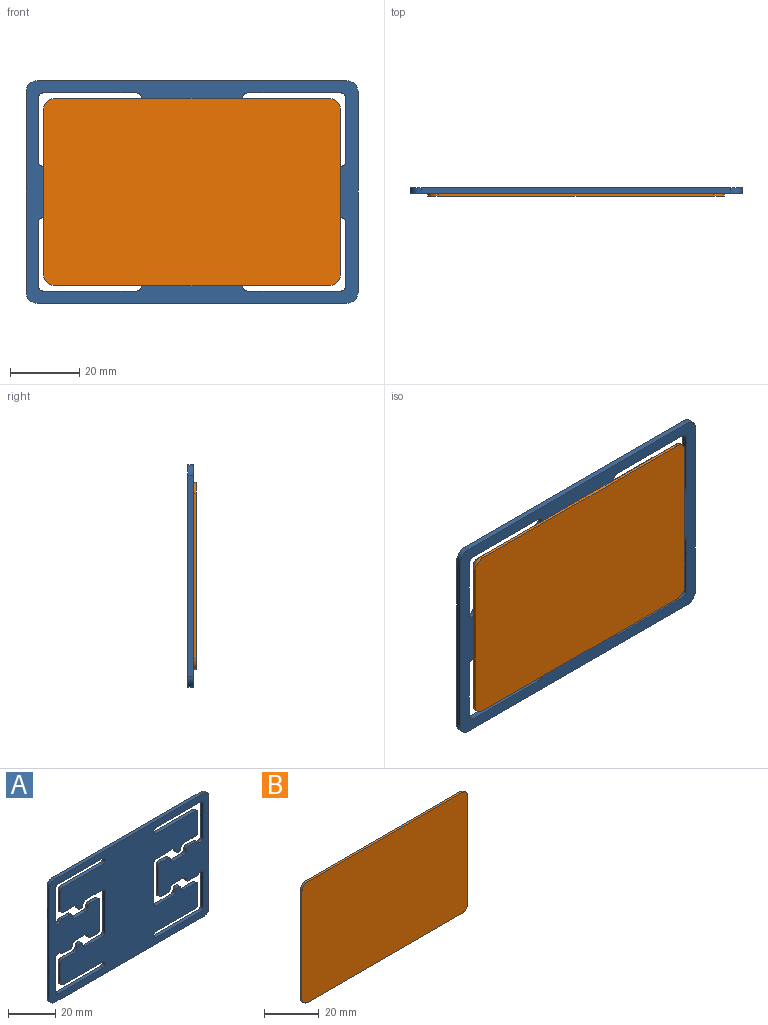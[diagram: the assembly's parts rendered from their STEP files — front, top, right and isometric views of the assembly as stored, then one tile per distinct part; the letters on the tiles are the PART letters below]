
ASSEMBLY  parts=2 mates=1
PART A: 110 faces, bbox 95.8x1.6x64.1 mm
  f0: plane 95.76x64.14mm, normal (0,1,0), area 4997.3mm2, adj f2,f3,f4,f5,f6,f7,f8,f9
  f1: plane 95.76x64.14mm, normal (0,-1,0), area 4997.3mm2, adj f2,f3,f4,f5,f6,f7,f8,f9
  f2: cylinder r=3.17mm len=3.18mm, axis (0,1,0), area 8mm2, adj f0,f1,f3,f9
  f3: plane 89.41x1.6mm, normal (0,0,-1), area 143.1mm2, adj f0,f1,f2,f4
  f4: cylinder r=3.17mm len=3.18mm, axis (0,-1,0), area 8mm2, adj f0,f1,f3,f5
  f5: plane 57.79x1.6mm, normal (1,0,0), area 92.5mm2, adj f0,f1,f4,f6
  f6: cylinder r=3.17mm len=3.18mm, axis (0,1,0), area 8mm2, adj f0,f1,f5,f7
  f7: plane 89.41x1.6mm, normal (0,0,1), area 143.1mm2, adj f0,f1,f6,f8
  f8: cylinder r=3.17mm len=3.18mm, axis (0,-1,0), area 8mm2, adj f0,f1,f7,f9
  f9: plane 57.79x1.6mm, normal (-1,0,0), area 92.5mm2, adj f0,f1,f2,f8
  f10: plane 3.81x1.6mm, normal (0,0,-1), area 6.1mm2, adj f0,f1,f54,f55
  f11: plane 14.82x1.6mm, normal (1,0,0), area 23.7mm2, adj f0,f1,f46,f54
  f12: plane 3.81x1.6mm, normal (0,0,1), area 6.1mm2, adj f0,f1,f46,f47
  f13: cylinder r=1.59mm len=1.6mm, axis (0,1,0), area 4mm2, adj f0,f1,f14,f47
  f14: plane 6.35x1.6mm, normal (0,0,1), area 10.2mm2, adj f0,f1,f13,f15
  f15: cylinder r=1.59mm len=1.6mm, axis (0,1,0), area 4mm2, adj f0,f1,f14,f49
  f16: plane 4.24x1.6mm, normal (0,0,1), area 6.8mm2, adj f0,f1,f49,f56
  f17: cylinder r=1.59mm len=2.96mm, axis (0,1,0), area 6.7mm2, adj f0,f1,f18,f56
  f18: plane 17.99x1.6mm, normal (1,0,0), area 28.8mm2, adj f0,f1,f17,f19
  f19: cylinder r=1.59mm len=1.6mm, axis (0,1,0), area 4mm2, adj f0,f1,f18,f20
  f20: plane 26.67x1.6mm, normal (0,0,-1), area 42.7mm2, adj f0,f1,f19,f21
  f21: cylinder r=1.59mm len=3.18mm, axis (0,1,0), area 8mm2, adj f0,f1,f20,f22
  f22: plane 23.5x1.6mm, normal (0,0,1), area 37.6mm2, adj f0,f1,f21,f50
  f23: plane 10.05x1.6mm, normal (-1,0,0), area 16.1mm2, adj f0,f1,f50,f57
  f24: plane 6.99x1.6mm, normal (0,0,-1), area 11.2mm2, adj f0,f1,f25,f57
  f25: cylinder r=1.59mm len=1.6mm, axis (0,1,0), area 4mm2, adj f0,f1,f24,f48
  f26: cylinder r=1.59mm len=1.6mm, axis (0,1,0), area 4mm2, adj f0,f1,f27,f48
  f27: plane 10.16x1.6mm, normal (0,0,-1), area 16.3mm2, adj f0,f1,f26,f28
  f28: cylinder r=1.59mm len=1.6mm, axis (0,1,0), area 4mm2, adj f0,f1,f27,f29
  f29: plane 21.17x1.6mm, normal (-1,0,0), area 33.9mm2, adj f0,f1,f28,f30
  f30: cylinder r=1.59mm len=1.6mm, axis (0,1,0), area 4mm2, adj f0,f1,f29,f31
  f31: plane 10.16x1.6mm, normal (0,0,1), area 16.3mm2, adj f0,f1,f30,f32
  f32: cylinder r=1.59mm len=1.6mm, axis (0,1,0), area 4mm2, adj f0,f1,f31,f53
  f33: cylinder r=1.59mm len=1.6mm, axis (0,1,0), area 4mm2, adj f0,f1,f34,f53
  f34: plane 6.99x1.6mm, normal (0,0,1), area 11.2mm2, adj f0,f1,f33,f59
  f35: plane 10.05x1.6mm, normal (-1,0,0), area 16.1mm2, adj f0,f1,f51,f59
  f36: plane 23.5x1.6mm, normal (0,0,-1), area 37.6mm2, adj f0,f1,f37,f51
  f37: cylinder r=1.59mm len=3.18mm, axis (0,1,0), area 8mm2, adj f0,f1,f36,f38
  f38: plane 26.67x1.6mm, normal (0,0,1), area 42.7mm2, adj f0,f1,f37,f39
  f39: cylinder r=1.59mm len=1.6mm, axis (0,1,0), area 4mm2, adj f0,f1,f38,f40
  f40: plane 17.99x1.6mm, normal (1,0,0), area 28.8mm2, adj f0,f1,f39,f41
  f41: cylinder r=1.59mm len=2.96mm, axis (0,1,0), area 6.7mm2, adj f0,f1,f40,f58
  f42: plane 4.24x1.6mm, normal (0,0,-1), area 6.8mm2, adj f0,f1,f52,f58
  f43: cylinder r=1.59mm len=1.6mm, axis (0,1,0), area 4mm2, adj f0,f1,f44,f52
  f44: plane 6.35x1.6mm, normal (0,0,-1), area 10.2mm2, adj f0,f1,f43,f45
  f45: cylinder r=1.59mm len=1.6mm, axis (0,1,0), area 4mm2, adj f0,f1,f44,f55
  f46: cylinder r=1.59mm len=1.6mm, axis (0,1,0), area 4mm2, adj f0,f1,f11,f12
  f47: cylinder r=1.59mm len=1.6mm, axis (0,1,0), area 4mm2, adj f0,f1,f12,f13
  f48: cylinder r=1.59mm len=3.18mm, axis (0,1,0), area 8mm2, adj f0,f1,f25,f26
  f49: cylinder r=1.59mm len=1.6mm, axis (0,1,0), area 4mm2, adj f0,f1,f15,f16
  f50: cylinder r=1.59mm len=1.6mm, axis (0,1,0), area 4mm2, adj f0,f1,f22,f23
  f51: cylinder r=1.59mm len=1.6mm, axis (0,1,0), area 4mm2, adj f0,f1,f35,f36
  f52: cylinder r=1.59mm len=1.6mm, axis (0,1,0), area 4mm2, adj f0,f1,f42,f43
  f53: cylinder r=1.59mm len=3.18mm, axis (0,1,0), area 8mm2, adj f0,f1,f32,f33
  f54: cylinder r=1.59mm len=1.6mm, axis (0,-1,0), area 4mm2, adj f0,f1,f10,f11
  f55: cylinder r=1.59mm len=1.6mm, axis (0,1,0), area 4mm2, adj f0,f1,f10,f45
  f56: cylinder r=1.59mm len=1.6mm, axis (0,1,0), area 2.7mm2, adj f0,f1,f16,f17
  f57: cylinder r=1.59mm len=1.6mm, axis (0,1,0), area 4mm2, adj f0,f1,f23,f24
  f58: cylinder r=1.59mm len=1.6mm, axis (0,1,0), area 2.7mm2, adj f0,f1,f41,f42
  f59: cylinder r=1.59mm len=1.6mm, axis (0,1,0), area 4mm2, adj f0,f1,f34,f35
  f60: plane 3.81x1.6mm, normal (0,0,-1), area 6.1mm2, adj f0,f1,f104,f105
  f61: cylinder r=1.59mm len=1.6mm, axis (0,1,0), area 4mm2, adj f0,f1,f62,f105
  f62: plane 6.35x1.6mm, normal (0,0,-1), area 10.2mm2, adj f0,f1,f61,f63
  f63: cylinder r=1.59mm len=1.6mm, axis (0,1,0), area 4mm2, adj f0,f1,f62,f102
  f64: plane 4.24x1.6mm, normal (0,0,-1), area 6.8mm2, adj f0,f1,f102,f108
  f65: cylinder r=1.59mm len=2.96mm, axis (0,1,0), area 6.7mm2, adj f0,f1,f66,f108
  f66: plane 17.99x1.6mm, normal (-1,0,0), area 28.8mm2, adj f0,f1,f65,f67
  f67: cylinder r=1.59mm len=1.6mm, axis (0,1,0), area 4mm2, adj f0,f1,f66,f68
  f68: plane 26.67x1.6mm, normal (0,0,1), area 42.7mm2, adj f0,f1,f67,f69
  f69: cylinder r=1.59mm len=3.18mm, axis (0,1,0), area 8mm2, adj f0,f1,f68,f70
  f70: plane 23.5x1.6mm, normal (0,0,-1), area 37.6mm2, adj f0,f1,f69,f101
  f71: plane 10.05x1.6mm, normal (1,0,0), area 16.1mm2, adj f0,f1,f101,f109
  f72: plane 6.99x1.6mm, normal (0,0,1), area 11.2mm2, adj f0,f1,f73,f109
  f73: cylinder r=1.59mm len=1.6mm, axis (0,1,0), area 4mm2, adj f0,f1,f72,f103
  f74: cylinder r=1.59mm len=1.6mm, axis (0,1,0), area 4mm2, adj f0,f1,f75,f103
  f75: plane 10.16x1.6mm, normal (0,0,1), area 16.3mm2, adj f0,f1,f74,f76
  f76: cylinder r=1.59mm len=1.6mm, axis (0,1,0), area 4mm2, adj f0,f1,f75,f77
  f77: plane 21.17x1.6mm, normal (1,0,0), area 33.9mm2, adj f0,f1,f76,f78
  f78: cylinder r=1.59mm len=1.6mm, axis (0,1,0), area 4mm2, adj f0,f1,f77,f79
  f79: plane 10.16x1.6mm, normal (0,0,-1), area 16.3mm2, adj f0,f1,f78,f80
  f80: cylinder r=1.59mm len=1.6mm, axis (0,1,0), area 4mm2, adj f0,f1,f79,f98
  f81: cylinder r=1.59mm len=1.6mm, axis (0,1,0), area 4mm2, adj f0,f1,f82,f98
  f82: plane 6.99x1.6mm, normal (0,0,-1), area 11.2mm2, adj f0,f1,f81,f107
  f83: plane 10.05x1.6mm, normal (1,0,0), area 16.1mm2, adj f0,f1,f100,f107
  f84: plane 23.5x1.6mm, normal (0,0,1), area 37.6mm2, adj f0,f1,f85,f100
  f85: cylinder r=1.59mm len=3.18mm, axis (0,1,0), area 8mm2, adj f0,f1,f84,f86
  f86: plane 26.67x1.6mm, normal (0,0,-1), area 42.7mm2, adj f0,f1,f85,f87
  f87: cylinder r=1.59mm len=1.6mm, axis (0,1,0), area 4mm2, adj f0,f1,f86,f88
  f88: plane 17.99x1.6mm, normal (-1,0,0), area 28.8mm2, adj f0,f1,f87,f89
  f89: cylinder r=1.59mm len=2.96mm, axis (0,1,0), area 6.7mm2, adj f0,f1,f88,f106
  f90: plane 4.24x1.6mm, normal (0,0,1), area 6.8mm2, adj f0,f1,f99,f106
  f91: cylinder r=1.59mm len=1.6mm, axis (0,1,0), area 4mm2, adj f0,f1,f92,f99
  f92: plane 6.35x1.6mm, normal (0,0,1), area 10.2mm2, adj f0,f1,f91,f93
  f93: cylinder r=1.59mm len=1.6mm, axis (0,1,0), area 4mm2, adj f0,f1,f92,f97
  f94: plane 3.81x1.6mm, normal (0,0,1), area 6.1mm2, adj f0,f1,f96,f97
  f95: plane 14.82x1.6mm, normal (-1,0,0), area 23.7mm2, adj f0,f1,f96,f104
  f96: cylinder r=1.59mm len=1.6mm, axis (0,1,0), area 4mm2, adj f0,f1,f94,f95
  f97: cylinder r=1.59mm len=1.6mm, axis (0,1,0), area 4mm2, adj f0,f1,f93,f94
  f98: cylinder r=1.59mm len=3.18mm, axis (0,1,0), area 8mm2, adj f0,f1,f80,f81
  f99: cylinder r=1.59mm len=1.6mm, axis (0,1,0), area 4mm2, adj f0,f1,f90,f91
  f100: cylinder r=1.59mm len=1.6mm, axis (0,1,0), area 4mm2, adj f0,f1,f83,f84
  f101: cylinder r=1.59mm len=1.6mm, axis (0,1,0), area 4mm2, adj f0,f1,f70,f71
  f102: cylinder r=1.59mm len=1.6mm, axis (0,1,0), area 4mm2, adj f0,f1,f63,f64
  f103: cylinder r=1.59mm len=3.18mm, axis (0,1,0), area 8mm2, adj f0,f1,f73,f74
  f104: cylinder r=1.59mm len=1.6mm, axis (0,-1,0), area 4mm2, adj f0,f1,f60,f95
  f105: cylinder r=1.59mm len=1.6mm, axis (0,1,0), area 4mm2, adj f0,f1,f60,f61
  f106: cylinder r=1.59mm len=1.6mm, axis (0,1,0), area 2.7mm2, adj f0,f1,f89,f90
  f107: cylinder r=1.59mm len=1.6mm, axis (0,1,0), area 4mm2, adj f0,f1,f82,f83
  f108: cylinder r=1.59mm len=1.6mm, axis (0,1,0), area 2.7mm2, adj f0,f1,f64,f65
  f109: cylinder r=1.59mm len=1.6mm, axis (0,1,0), area 4mm2, adj f0,f1,f71,f72
PART B: 10 faces, bbox 85.6x0.8x54 mm
  f0: plane 79.25x0.83mm, normal (0,0,1), area 65.4mm2, adj f1,f7,f8,f9
  f1: cylinder r=3.17mm len=3.18mm, axis (0,1,0), area 4.1mm2, adj f0,f2,f8,f9
  f2: plane 47.63x0.83mm, normal (-1,0,0), area 39.3mm2, adj f1,f3,f8,f9
  f3: cylinder r=3.17mm len=3.18mm, axis (0,1,0), area 4.1mm2, adj f2,f4,f8,f9
  f4: plane 79.25x0.83mm, normal (0,0,-1), area 65.4mm2, adj f3,f5,f8,f9
  f5: cylinder r=3.17mm len=3.18mm, axis (0,1,0), area 4.1mm2, adj f4,f6,f8,f9
  f6: plane 47.63x0.83mm, normal (1,0,0), area 39.3mm2, adj f5,f7,f8,f9
  f7: cylinder r=3.17mm len=3.18mm, axis (0,1,0), area 4.1mm2, adj f0,f6,f8,f9
  f8: plane 85.6x53.98mm, normal (0,-1,0), area 4611.5mm2, adj f0,f1,f2,f3,f4,f5,f6,f7
  f9: plane 85.6x53.98mm, normal (0,1,0), area 4611.5mm2, adj f0,f1,f2,f3,f4,f5,f6,f7
PLACE A t=(-16.51,-1.6,-19.58)mm
PLACE B rot(axis=(1,0,0),180deg) t=(-16.51,-2.43,34.4)mm
MATE fastened B.f8 <-> A.f1  axis (0,1,0) through (26.29,-1.6,7.41)mm
